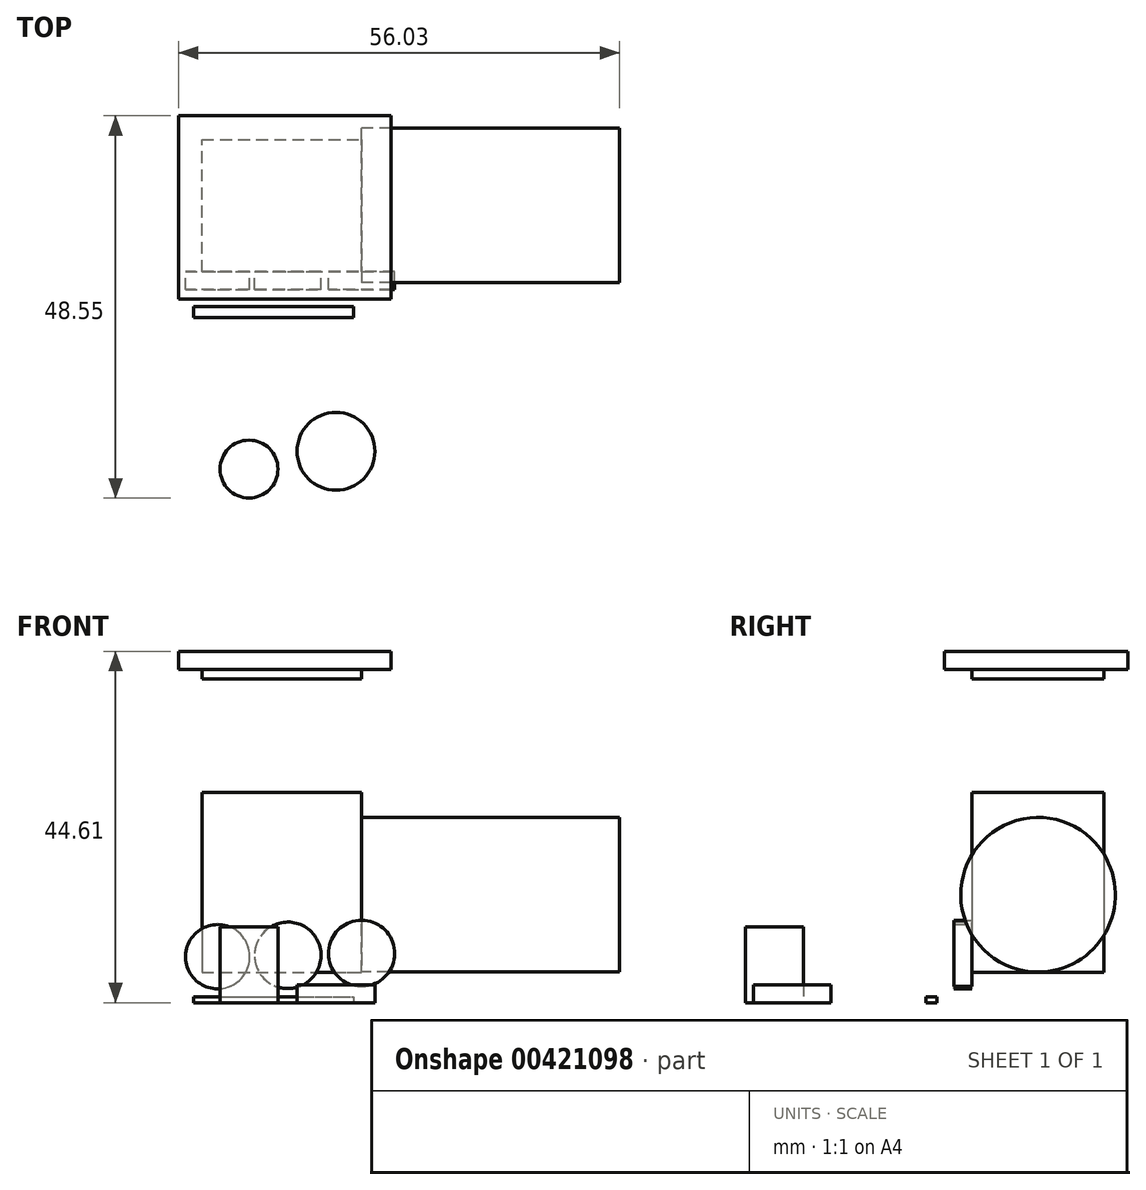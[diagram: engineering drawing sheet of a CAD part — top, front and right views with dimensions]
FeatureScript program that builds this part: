
annotation { "Feature Type Name" : "Feature", "Feature Type Description" : "" }
export const myFeature = defineFeature(function(context is Context, id is Id, definition is map)
    precondition{}
    {
        {
            var Q0;
            Q0=qCreatedBy(makeId("Front.planeOp"),FACE);
            var sketch = newSketch(context, id + "F0", { "sketchPlane" : qUnion([Q0])});
            skLineSegment(sketch, "E0.bottom", {"start": v(-55.86, 44.61) * mm, "end": v(-35.58, 44.61) * mm});
            skLineSegment(sketch, "E0.top", {"start": v(-55.86, 41.11) * mm, "end": v(-35.58, 41.11) * mm});
            skLineSegment(sketch, "E0.left", {"start": v(-55.86, 44.61) * mm, "end": v(-55.86, 41.11) * mm});
            skLineSegment(sketch, "E0.right", {"start": v(-35.58, 44.61) * mm, "end": v(-35.58, 41.11) * mm});
            skLineSegment(sketch, "E1.bottom", {"start": v(-40.37, 41.11) * mm, "end": v(-35.58, 41.11) * mm});
            skLineSegment(sketch, "E1.top", {"start": v(-40.37, 26.73) * mm, "end": v(-35.58, 26.73) * mm});
            skLineSegment(sketch, "E1.left", {"start": v(-40.37, 41.11) * mm, "end": v(-40.37, 26.73) * mm});
            skLineSegment(sketch, "E1.right", {"start": v(-35.58, 41.11) * mm, "end": v(-35.58, 26.73) * mm});
            skLineSegment(sketch, "E2.bottom", {"start": v(-55.86, 41.11) * mm, "end": v(-50.51, 41.11) * mm});
            skLineSegment(sketch, "E2.top", {"start": v(-55.86, 26.73) * mm, "end": v(-50.51, 26.73) * mm});
            skLineSegment(sketch, "E2.left", {"start": v(-55.86, 41.11) * mm, "end": v(-55.86, 26.73) * mm});
            skLineSegment(sketch, "E2.right", {"start": v(-50.51, 41.11) * mm, "end": v(-50.51, 26.73) * mm});
            skLineSegment(sketch, "E3.bottom", {"start": v(-55.86, 26.73) * mm, "end": v(-35.58, 26.73) * mm});
            skLineSegment(sketch, "E3.top", {"start": v(-55.86, 3.87) * mm, "end": v(-35.58, 3.87) * mm});
            skLineSegment(sketch, "E3.left", {"start": v(-55.86, 26.73) * mm, "end": v(-55.86, 3.87) * mm});
            skLineSegment(sketch, "E3.right", {"start": v(-35.58, 26.73) * mm, "end": v(-35.58, 3.87) * mm});
            skSolve(sketch);
        }
        {
            var Q0;
            Q0=makeQuery(id+"F0.imprint","IMPRINT",FACE,{"disambiguationData":[TD([[makeQuery(id+"F0.imprint","IMPRINT",EDGE,{"derivedFrom":sQuery(id+"F0.wireOp",EDGE,"E3.top")}),1.0]])]});
            var Q1;
            Q1=makeQuery(id+"F0.imprint","IMPRINT",FACE,{"disambiguationData":[TD([[makeQuery(id+"F0.imprint","IMPRINT",EDGE,{"derivedFrom":sQuery(id+"F0.wireOp",EDGE,"E2.bottom")}),-1.0]])]});
            var Q2;
            Q2=makeQuery(id+"F0.imprint","IMPRINT",FACE,{"disambiguationData":[TD([[makeQuery(id+"F0.imprint","IMPRINT",EDGE,{"derivedFrom":sQuery(id+"F0.wireOp",EDGE,"E1.bottom")}),-1.0]])]});
            var Q3;
            Q3=makeQuery(id+"F0.imprint","IMPRINT",FACE,{"disambiguationData":[TD([[makeQuery(id+"F0.imprint","IMPRINT",EDGE,{"derivedFrom":sQuery(id+"F0.wireOp",EDGE,"E0.bottom")}),-1.0]])]});
            extrude(context, id + "F1", {"entities" : qUnion([Q0, Q1, Q2, Q3]), "depth" : 16.76 * mm});
        }
        {
            var Q0;
            Q0=makeQuery(id+"F1.opExtrude","SWEPT_FACE",FACE,{"disambiguationData":[OSD([sQuery(id+"F0.wireOp",EDGE,"E0.right"),sQuery(id+"F0.wireOp",EDGE,"E1.right"),sQuery(id+"F0.wireOp",EDGE,"E3.right")])]});
            var sketch = newSketch(context, id + "F2", { "sketchPlane" : qUnion([Q0])});
            skCircle(sketch, "E4", {"center": v(-8.34, 13.7) * mm, "radius": 9.82 * mm});
            skSolve(sketch);
        }
        {
            var Q0;
            {var subQ0=sQuery(id+"F2.wireOp",EDGE,"E4");var subQ1=sQuery(id+"F0.wireOp",EDGE,"E3.right");var subQ2=sQuery(id+"F0.wireOp",EDGE,"E1.right");var subQ3=sQuery(id+"F0.wireOp",EDGE,"E0.right");var subQ4=makeQuery(id+"F1.opExtrude","CAP_EDGE",EDGE,{"disambiguationData":[OSD([subQ3,subQ2,subQ1])],"isStart":false});var subQ5=makeQuery(id+"F2.imprint","INTERSECT",VERTEX,{"disambiguationData":[OD(0.0)],"derivedFrom":[subQ4,subQ0]});Q0=makeQuery(id+"F2.imprint","IMPRINT",FACE,{"disambiguationData":[TD([[makeQuery(id+"F2.imprint","IMPRINT",EDGE,{"disambiguationData":[TD([[subQ5,1.0]])],"derivedFrom":subQ0}),1.0]])]});}
            extrude(context, id + "F3", {"entities" : qUnion([Q0]), "operationType" : NewBodyOperationType.ADD, "depth" : 32.77 * mm});
        }
        {
            var Q0;
            {var subQ0=sQuery(id+"F2.wireOp",EDGE,"E4");var subQ1=sQuery(id+"F0.wireOp",EDGE,"E3.right");var subQ2=sQuery(id+"F0.wireOp",EDGE,"E1.right");var subQ3=sQuery(id+"F0.wireOp",EDGE,"E0.right");var subQ4=makeQuery(id+"F1.opExtrude","CAP_EDGE",EDGE,{"disambiguationData":[OSD([subQ3,subQ2,subQ1])],"isStart":false});Q0=makeQuery(id+"F3.boolean.opBoolean","MERGE",FACE,{"derivedFrom":[makeQuery(id+"F1.opExtrude","CAP_FACE",FACE,{"disambiguationData":[OSD([sQuery(id+"F0.wireOp",EDGE,"E0.bottom"),sQuery(id+"F0.wireOp",EDGE,"E0.top"),sQuery(id+"F0.wireOp",EDGE,"E0.left"),subQ3,sQuery(id+"F0.wireOp",EDGE,"E1.left"),subQ2,sQuery(id+"F0.wireOp",EDGE,"E2.left"),sQuery(id+"F0.wireOp",EDGE,"E2.right"),sQuery(id+"F0.wireOp",EDGE,"E3.bottom"),sQuery(id+"F0.wireOp",EDGE,"E3.top"),sQuery(id+"F0.wireOp",EDGE,"E3.left"),subQ1])],"isStart":false}),makeQuery(id+"F3.opExtrude","SWEPT_FACE",FACE,{"disambiguationData":[OSD([subQ3,subQ2,subQ1]),TDD([makeQuery(id+"F2.imprint","IMPRINT",EDGE,{"disambiguationData":[TD([[makeQuery(id+"F2.imprint","INTERSECT",VERTEX,{"disambiguationData":[OD(0.0)],"derivedFrom":[subQ4,subQ0]}),-1.0]])],"derivedFrom":subQ4})])]})]});}
            var sketch = newSketch(context, id + "F4", { "sketchPlane" : qUnion([Q0])});
            skCircle(sketch, "E5", {"center": v(-53.87, 5.84) * mm, "radius": 4.09 * mm});
            skCircle(sketch, "E6", {"center": v(-44.95, 6.01) * mm, "radius": 4.22 * mm});
            skCircle(sketch, "E7", {"center": v(-35.58, 6.27) * mm, "radius": 4.2 * mm});
            skSolve(sketch);
        }
        {
            var Q0;
            {var subQ0=sQuery(id+"F4.wireOp",EDGE,"E5");var subQ3=makeQuery(id+"F1.opExtrude","CAP_EDGE",EDGE,{"disambiguationData":[OSD([sQuery(id+"F0.wireOp",EDGE,"E3.top")])],"isStart":false});var subQ4=makeQuery(id+"F4.imprint","INTERSECT",VERTEX,{"derivedFrom":[subQ3,subQ0]});Q0=makeQuery(id+"F4.imprint","IMPRINT",FACE,{"disambiguationData":[TD([[makeQuery(id+"F4.imprint","IMPRINT",EDGE,{"disambiguationData":[TD([[subQ4,1.0]])],"derivedFrom":subQ0}),1.0]])]});}
            var Q1;
            {var subQ0=sQuery(id+"F4.wireOp",EDGE,"E5");var subQ3=makeQuery(id+"F1.opExtrude","CAP_EDGE",EDGE,{"disambiguationData":[OSD([sQuery(id+"F0.wireOp",EDGE,"E3.top")])],"isStart":false});var subQ4=makeQuery(id+"F4.imprint","INTERSECT",VERTEX,{"derivedFrom":[subQ3,subQ0]});Q1=makeQuery(id+"F4.imprint","IMPRINT",FACE,{"disambiguationData":[TD([[makeQuery(id+"F4.imprint","IMPRINT",EDGE,{"disambiguationData":[TD([[subQ4,-1.0]])],"derivedFrom":subQ0}),1.0]])]});}
            var Q2;
            {var subQ0=sQuery(id+"F4.wireOp",EDGE,"E6");var subQ1=makeQuery(id+"F1.opExtrude","CAP_EDGE",EDGE,{"disambiguationData":[OSD([sQuery(id+"F0.wireOp",EDGE,"E3.top")])],"isStart":false});var subQ2=makeQuery(id+"F4.imprint","INTERSECT",VERTEX,{"disambiguationData":[OD(0.0)],"derivedFrom":[subQ1,subQ0]});Q2=makeQuery(id+"F4.imprint","IMPRINT",FACE,{"disambiguationData":[TD([[makeQuery(id+"F4.imprint","IMPRINT",EDGE,{"disambiguationData":[TD([[subQ2,-1.0]])],"derivedFrom":subQ0}),1.0]])]});}
            var Q3;
            {var subQ0=sQuery(id+"F4.wireOp",EDGE,"E6");var subQ1=makeQuery(id+"F1.opExtrude","CAP_EDGE",EDGE,{"disambiguationData":[OSD([sQuery(id+"F0.wireOp",EDGE,"E3.top")])],"isStart":false});var subQ2=makeQuery(id+"F4.imprint","INTERSECT",VERTEX,{"disambiguationData":[OD(0.0)],"derivedFrom":[subQ1,subQ0]});Q3=makeQuery(id+"F4.imprint","IMPRINT",FACE,{"disambiguationData":[TD([[makeQuery(id+"F4.imprint","IMPRINT",EDGE,{"disambiguationData":[TD([[subQ2,1.0]])],"derivedFrom":subQ0}),1.0]])]});}
            var Q4;
            {var subQ0=sQuery(id+"F4.wireOp",EDGE,"E7");var subQ9=sQuery(id+"F0.wireOp",EDGE,"E3.top");var subQ10=makeQuery(id+"F1.opExtrude","CAP_EDGE",EDGE,{"disambiguationData":[OSD([subQ9])],"isStart":false});var subQ11=makeQuery(id+"F4.imprint","INTERSECT",VERTEX,{"derivedFrom":[subQ10,subQ0]});Q4=makeQuery(id+"F4.imprint","IMPRINT",FACE,{"disambiguationData":[TD([[makeQuery(id+"F4.imprint","IMPRINT",EDGE,{"disambiguationData":[TD([[subQ11,-1.0]])],"derivedFrom":subQ0}),1.0]])]});}
            var Q5;
            {var subQ0=sQuery(id+"F4.wireOp",EDGE,"E7");var subQ9=sQuery(id+"F0.wireOp",EDGE,"E3.top");var subQ10=makeQuery(id+"F1.opExtrude","CAP_EDGE",EDGE,{"disambiguationData":[OSD([subQ9])],"isStart":false});var subQ11=makeQuery(id+"F4.imprint","INTERSECT",VERTEX,{"derivedFrom":[subQ10,subQ0]});Q5=makeQuery(id+"F4.imprint","IMPRINT",FACE,{"disambiguationData":[TD([[makeQuery(id+"F4.imprint","IMPRINT",EDGE,{"disambiguationData":[TD([[subQ11,1.0]])],"derivedFrom":subQ0}),1.0]])]});}
            extrude(context, id + "F5", {"entities" : qUnion([Q0, Q1, Q2, Q3, Q4, Q5]), "depth" : 2.3 * mm});
        }
        {
            var Q0;
            Q0=makeQuery(id+"F1.opExtrude","SWEPT_FACE",FACE,{"disambiguationData":[OSD([sQuery(id+"F0.wireOp",EDGE,"E0.bottom")])]});
            var sketch = newSketch(context, id + "F6", { "sketchPlane" : qUnion([Q0])});
            skLineSegment(sketch, "E8.bottom", {"start": v(-58.84, 3.05) * mm, "end": v(-31.83, 3.05) * mm});
            skLineSegment(sketch, "E8.top", {"start": v(-58.84, -20.22) * mm, "end": v(-31.83, -20.22) * mm});
            skLineSegment(sketch, "E8.left", {"start": v(-58.84, 3.05) * mm, "end": v(-58.84, -20.22) * mm});
            skLineSegment(sketch, "E8.right", {"start": v(-31.83, 3.05) * mm, "end": v(-31.83, -20.22) * mm});
            skSolve(sketch);
        }
        {
            var Q0;
            Q0=makeQuery(id+"F6.imprint","IMPRINT",FACE,{"disambiguationData":[TD([[makeQuery(id+"F6.imprint","IMPRINT",EDGE,{"derivedFrom":sQuery(id+"F6.wireOp",EDGE,"E8.bottom")}),-1.0]])]});
            extrude(context, id + "F7", {"entities" : qUnion([Q0]), "operationType" : NewBodyOperationType.ADD, "oppositeDirection" : true, "depth" : 2.3 * mm});
        }
        {
            var Q0;
            Q0=qCreatedBy(makeId("Top.planeOp"),FACE);
            var sketch = newSketch(context, id + "F8", { "sketchPlane" : qUnion([Q0])});
            skCircle(sketch, "E9", {"center": v(-49.88, -41.83) * mm, "radius": 3.67 * mm});
            skSolve(sketch);
        }
        {
            var Q0;
            Q0=makeQuery(id+"F8.imprint","IMPRINT",FACE,{"disambiguationData":[TD([[makeQuery(id+"F8.imprint","IMPRINT",EDGE,{"derivedFrom":sQuery(id+"F8.wireOp",EDGE,"E9")}),1.0]])]});
            extrude(context, id + "F9", {"entities" : qUnion([Q0]), "depth" : 9.65 * mm});
        }
        {
            var Q0;
            Q0=qCreatedBy(makeId("Top.planeOp"),FACE);
            var sketch = newSketch(context, id + "F10", { "sketchPlane" : qUnion([Q0])});
            skCircle(sketch, "E10", {"center": v(-38.83, -39.56) * mm, "radius": 4.94 * mm});
            skSolve(sketch);
        }
        {
            var Q0;
            Q0=makeQuery(id+"F10.imprint","IMPRINT",FACE,{"disambiguationData":[TD([[makeQuery(id+"F10.imprint","IMPRINT",EDGE,{"derivedFrom":sQuery(id+"F10.wireOp",EDGE,"E10")}),1.0]])]});
            extrude(context, id + "F11", {"entities" : qUnion([Q0]), "depth" : 2.3 * mm});
        }
        {
            var Q0;
            Q0=qCreatedBy(makeId("Top.planeOp"),FACE);
            var sketch = newSketch(context, id + "F12", { "sketchPlane" : qUnion([Q0])});
            skLineSegment(sketch, "E11.bottom", {"start": v(-56.91, -21.16) * mm, "end": v(-36.6, -21.16) * mm});
            skLineSegment(sketch, "E11.top", {"start": v(-56.91, -22.6) * mm, "end": v(-36.6, -22.6) * mm});
            skLineSegment(sketch, "E11.left", {"start": v(-56.91, -21.16) * mm, "end": v(-56.91, -22.6) * mm});
            skLineSegment(sketch, "E11.right", {"start": v(-36.6, -21.16) * mm, "end": v(-36.6, -22.6) * mm});
            skSolve(sketch);
        }
        {
            var Q0;
            Q0=makeQuery(id+"F12.imprint","IMPRINT",FACE,{"disambiguationData":[TD([[makeQuery(id+"F12.imprint","IMPRINT",EDGE,{"derivedFrom":sQuery(id+"F12.wireOp",EDGE,"E11.bottom")}),-1.0]])]});
            extrude(context, id + "F13", {"entities" : qUnion([Q0]), "depth" : 0.76 * mm});
        }
    });
